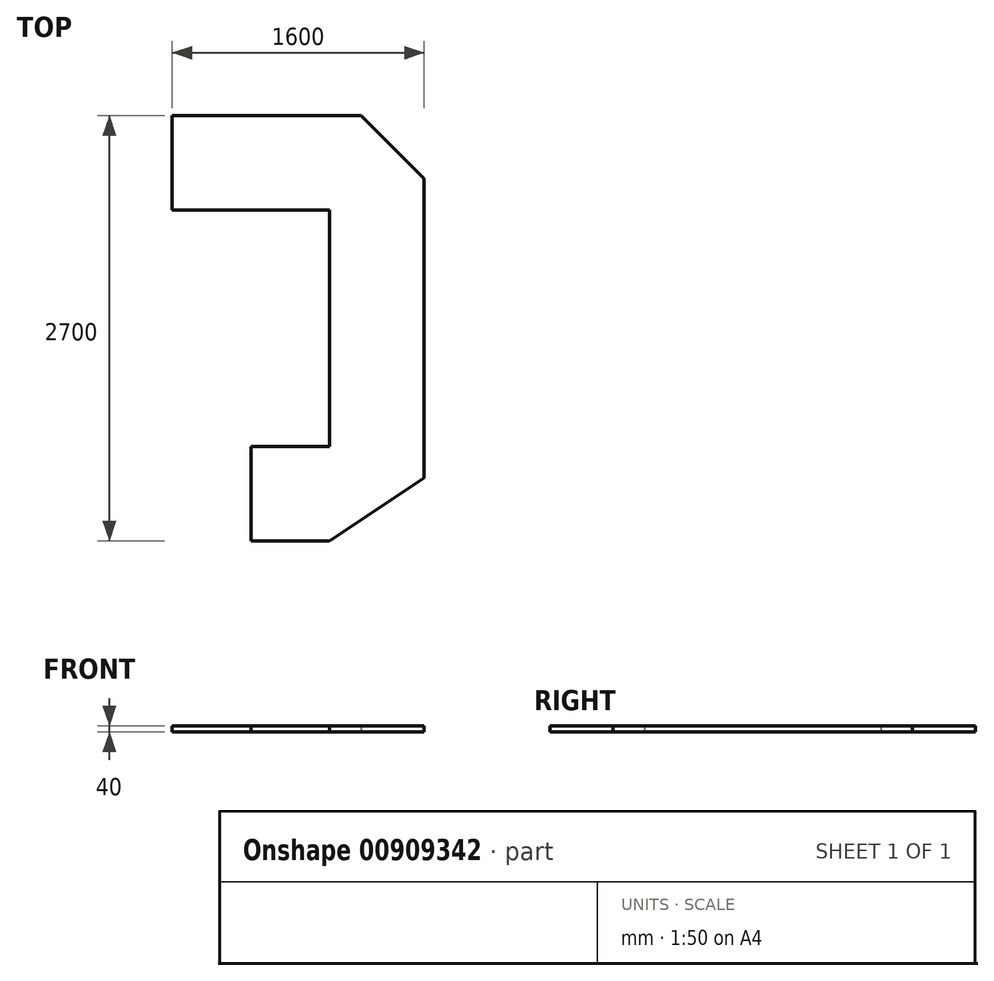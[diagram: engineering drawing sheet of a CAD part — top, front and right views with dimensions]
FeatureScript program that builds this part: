
annotation { "Feature Type Name" : "Feature", "Feature Type Description" : "" }
export const myFeature = defineFeature(function(context is Context, id is Id, definition is map)
    precondition{}
    {
        {
            var Q0;
            Q0=qCreatedBy(makeId("Top.planeOp"),FACE);
            var sketch = newSketch(context, id + "F0", { "sketchPlane" : qUnion([Q0])});
            skLineSegment(sketch, "E0", {"start": v(0, 0) * mm, "end": v(0, 600) * mm});
            skLineSegment(sketch, "E1", {"start": v(0, 600) * mm, "end": v(1200, 600) * mm});
            skLineSegment(sketch, "E2", {"start": v(1200, 600) * mm, "end": v(1600, 200) * mm});
            skLineSegment(sketch, "E3", {"start": v(1600, 200) * mm, "end": v(1600, -1700) * mm});
            skLineSegment(sketch, "E4", {"start": v(1600, -1700) * mm, "end": v(1000, -2100) * mm});
            skLineSegment(sketch, "E5", {"start": v(1000, -2100) * mm, "end": v(500, -2100) * mm});
            skLineSegment(sketch, "E6", {"start": v(500, -2100) * mm, "end": v(500, -1500) * mm});
            skLineSegment(sketch, "E7", {"start": v(500, -1500) * mm, "end": v(1000, -1500) * mm});
            skLineSegment(sketch, "E8", {"start": v(1000, -1500) * mm, "end": v(1000, 0) * mm});
            skLineSegment(sketch, "E9", {"start": v(1000, 0) * mm, "end": v(0, 0) * mm});
            skSolve(sketch);
        }
        {
            var Q0;
            Q0 = qSketchRegion(id + "F0", true);
            extrude(context, id + "F1", {"entities" : qUnion([Q0]), "depth" : 40 * mm, "offsetDistance" : 25 * mm});
        }
    });
